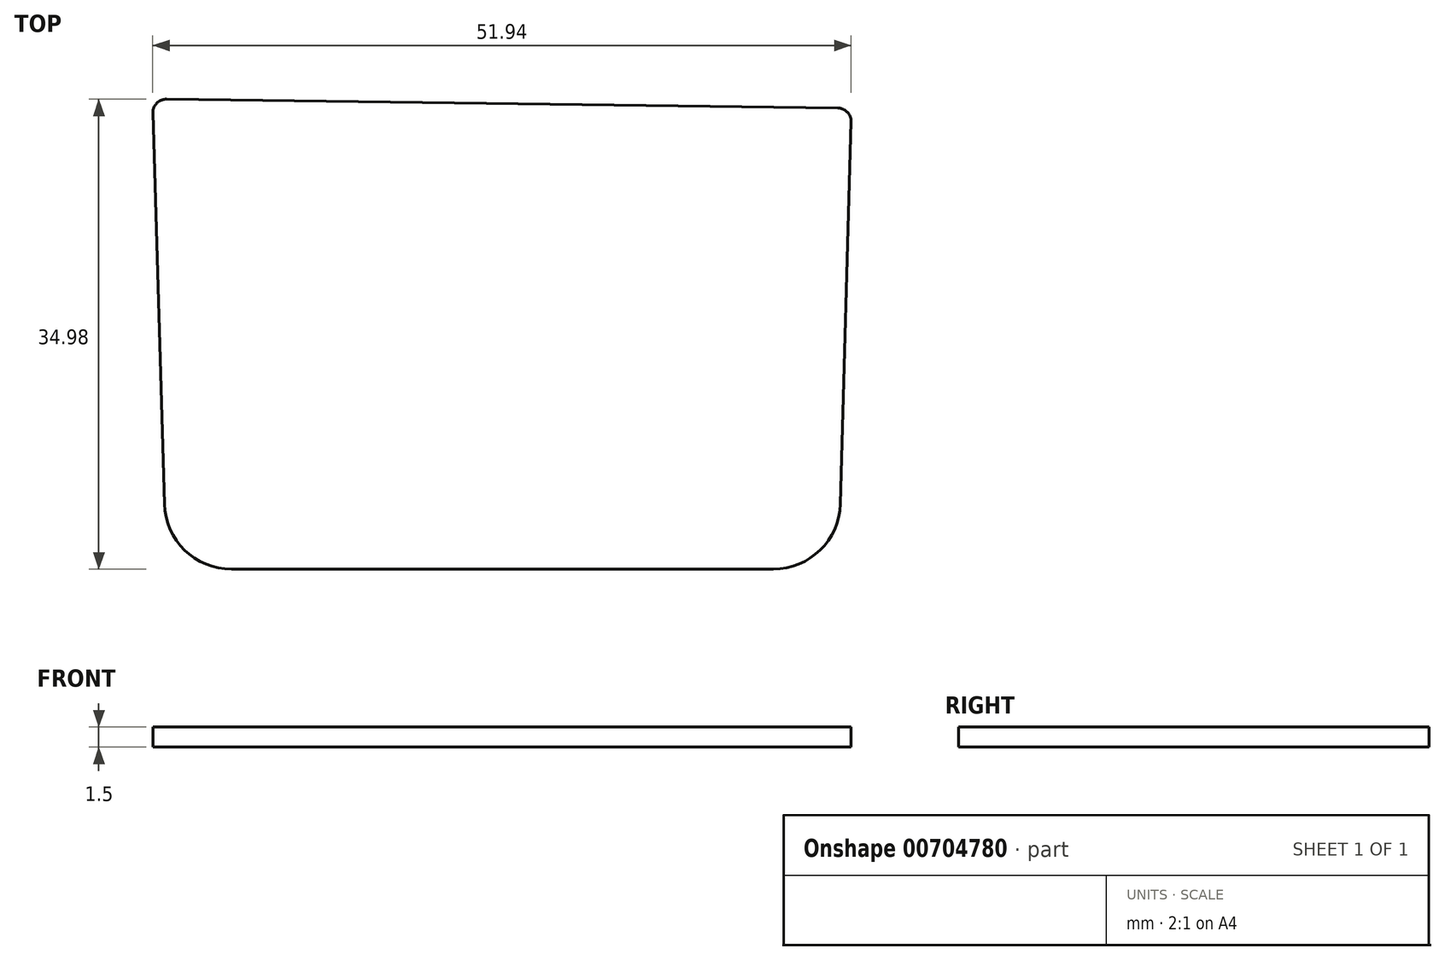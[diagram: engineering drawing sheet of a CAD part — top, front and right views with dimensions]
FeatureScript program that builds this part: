
annotation { "Feature Type Name" : "Feature", "Feature Type Description" : "" }
export const myFeature = defineFeature(function(context is Context, id is Id, definition is map)
    precondition{}
    {
        {
            var Q0;
            Q0=qCreatedBy(makeId("Top.planeOp"),FACE);
            var sketch = newSketch(context, id + "F0", { "sketchPlane" : qUnion([Q0])});
            skLineSegment(sketch, "E0", {"start": v(-20.6, 17.04) * mm, "end": v(19.67, 17.04) * mm});
            skLineSegment(sketch, "E1", {"start": v(-0.46, 17.04) * mm, "end": v(0, 52.04) * mm, "construction": true});
            skLineSegment(sketch, "E2", {"start": v(-25.45, 52.02) * mm, "end": v(24.49, 51.36) * mm});
            skLineSegment(sketch, "E3", {"start": v(25.47, 50.33) * mm, "end": v(24.67, 21.9) * mm});
            skLineSegment(sketch, "E4", {"start": v(-26.46, 51) * mm, "end": v(-25.6, 21.9) * mm});
            skPoint(sketch, "E5.visualSharp", {"position": v(24.54, 17.04) * mm});
            skArc(sketch, "E5.filletArc", {"start": v(19.67, 17.04) * mm, "mid": v(23.16, 18.46) * mm, "end": v(24.67, 21.9) * mm});
            skPoint(sketch, "E6.visualSharp", {"position": v(-25.46, 17.04) * mm});
            skArc(sketch, "E6.filletArc", {"start": v(-25.6, 21.9) * mm, "mid": v(-24.1, 18.45) * mm, "end": v(-20.6, 17.04) * mm});
            skPoint(sketch, "E7.visualSharp", {"position": v(25.5, 51.35) * mm});
            skArc(sketch, "E7.filletArc", {"start": v(25.47, 50.33) * mm, "mid": v(25.2, 51.06) * mm, "end": v(24.49, 51.36) * mm});
            skPoint(sketch, "E8.visualSharp", {"position": v(-26.5, 52.04) * mm});
            skArc(sketch, "E8.filletArc", {"start": v(-25.45, 52.02) * mm, "mid": v(-26.18, 51.73) * mm, "end": v(-26.46, 51) * mm});
            skSolve(sketch);
        }
        {
            var Q0;
            Q0=makeQuery(id+"F0.imprint","IMPRINT",FACE,{"disambiguationData":[TD([[makeQuery(id+"F0.imprint","IMPRINT",EDGE,{"derivedFrom":sQuery(id+"F0.wireOp",EDGE,"E0")}),1.0]])]});
            extrude(context, id + "F1", {"entities" : qUnion([Q0]), "depth" : 1.5 * mm, "offsetDistance" : 25 * mm});
        }
    });
